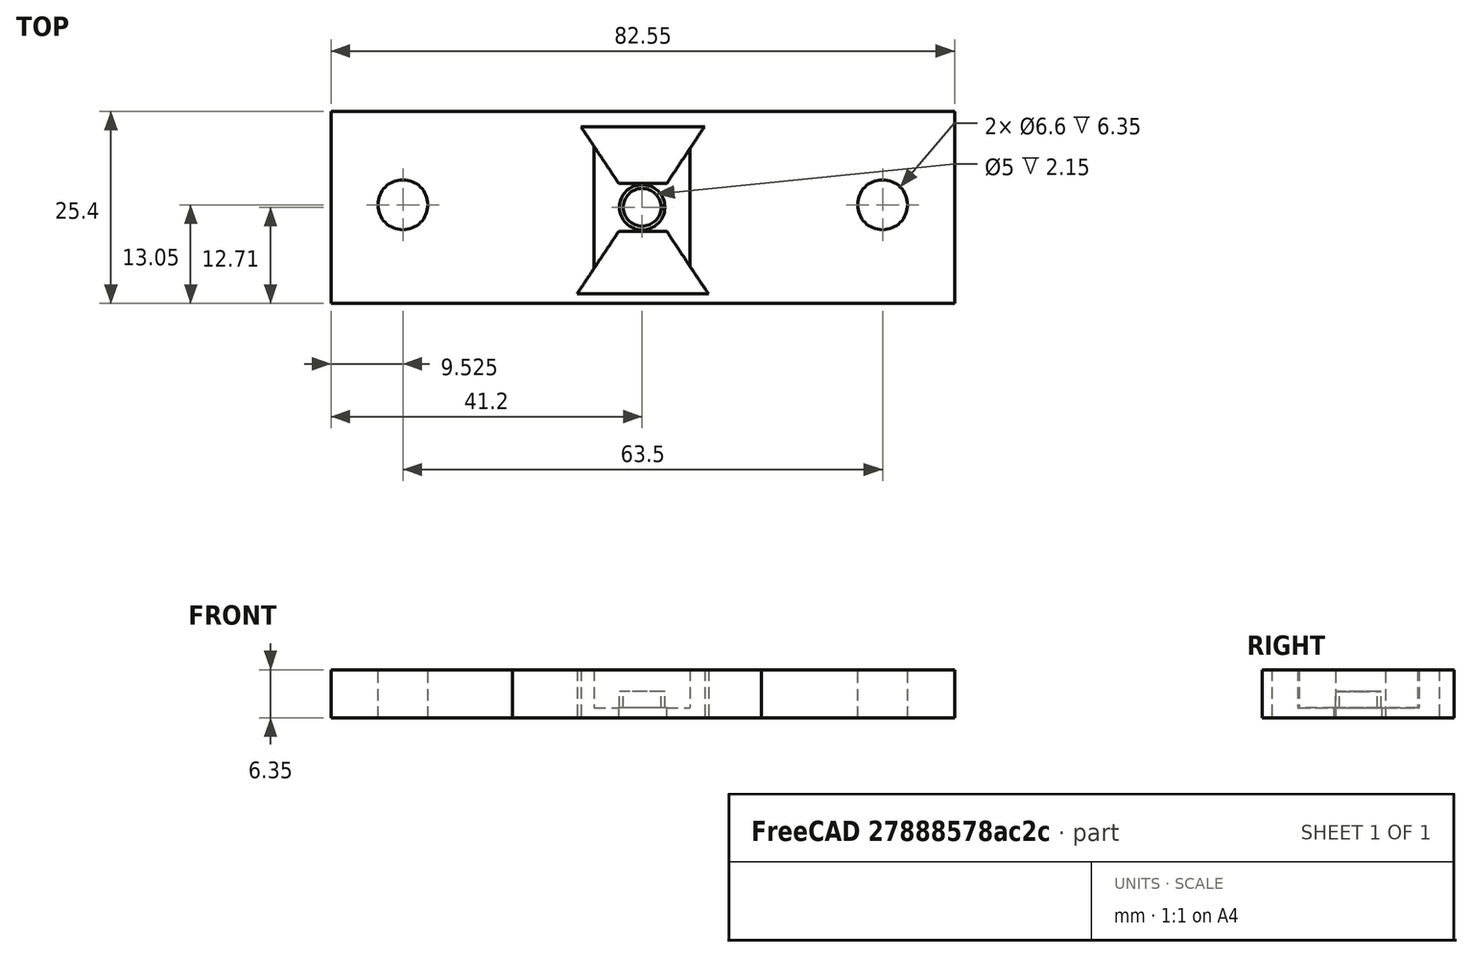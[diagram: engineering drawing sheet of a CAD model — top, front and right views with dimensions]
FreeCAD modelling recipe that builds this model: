
FCSTD DOCUMENT  (FreeCAD 0.16R6707 (Git))
Label: graphite
License: All rights reserved
LicenseURL: http://en.wikipedia.org/wiki/All_rights_reserved
objects: Part::Cylinder×4, Part::Box×3, Part::MultiFuse×2, Part::Cut×2, Path::FeaturePython×2, Part::Feature×1, Part::Extrusion×1, Path::FeatureCompoundPython×1
note: 13 computed .brp shape members not serialized (recipe doc carries the construction recipe); baked Part::Feature solids carry a one-line shape summary decoded from their .brp

FEATURE [Part::Cylinder] Cylinder  label="Hole1"
  Angle = 360
  Height = 10
  Placement = pos=(9.525,-12.7,1e-05) rot=(0,0,1;0rad)
  Radius = 3.302
FEATURE [Part::Cylinder] Cylinder001  label="Hole2"
  Angle = 360
  Height = 10
  Placement = pos=(73.025,-12.7,1e-05) rot=(0,0,1;0rad)
  Radius = 3.302
FEATURE [Part::Box] Box  label="Support1"
  Height = 6.35
  Length = 33
  Placement = pos=(24,-2.35,0) rot=(0,0,1;0rad)
  Width = 2
FEATURE [Part::Box] Box001  label="Support2"
  Height = 6.35
  Length = 33
  Placement = pos=(24,-25.753,0) rot=(0,0,1;0rad)
  Width = 1.25
FEATURE [Part::Box] Box002  label="Thinner"
  Height = 17
  Length = 12.7
  Placement = pos=(34.85,-21.35,1.35) rot=(0,0,1;0rad)
  Width = 16.7
FEATURE [Part::MultiFuse] Fusion
  Shapes = -> [Cylinder,Cylinder001,Box002]
FEATURE [Part::Feature] rect3338
  shape: bbox 82.55 x 25.4 x 2e-07 mm, 0 faces, 0 solids (baked)
FEATURE [Part::Extrusion] Extrude
  Base = -> rect3338
  Dir = (0,0,6.35)
  Solid = true
FEATURE [Part::Cut] Cut
  Base = -> Extrude
  Tool = -> Fusion
FEATURE [Part::Cylinder] Cylinder002  label="Cylinder"
  Angle = 360
  Height = 3.5
  Placement = pos=(41.2,-13.04,0) rot=(0,0,1;0rad)
  Radius = 3
FEATURE [Part::Cylinder] Cylinder003  label="Cylinder001"
  Angle = 360
  Height = 16
  Placement = pos=(41.2,-13.04,0) rot=(0,0,1;0rad)
  Radius = 2.5
FEATURE [Part::Cut] Cut001
  Base = -> Cylinder002
  Tool = -> Cylinder003
FEATURE [Part::MultiFuse] Fusion001
  Shapes = -> [Box001,Box,Cut,Cut001]
FEATURE [Path::FeaturePython] Machine  label="Machine_"  # Path/CAM operation (typed FeaturePython)
  MachineUnits = 0
  X = 0
  X_Max = 0
  X_Min = 0
  Y = 0
  Y_Max = 0
  Y_Min = 0
  Z = 0
  Z_Max = 0
  Z_Min = 0
FEATURE [Path::FeaturePython] Tool  label="Tool1"  # Path/CAM operation (typed FeaturePython)
  SpindleDir = 0
  SpindleSpeed = 0
  ToolNumber = 1
FEATURE [Path::FeatureCompoundPython] Project  # Path/CAM operation (typed FeaturePython)
  Group = -> [Machine,Tool]
  UsePlacements = false
